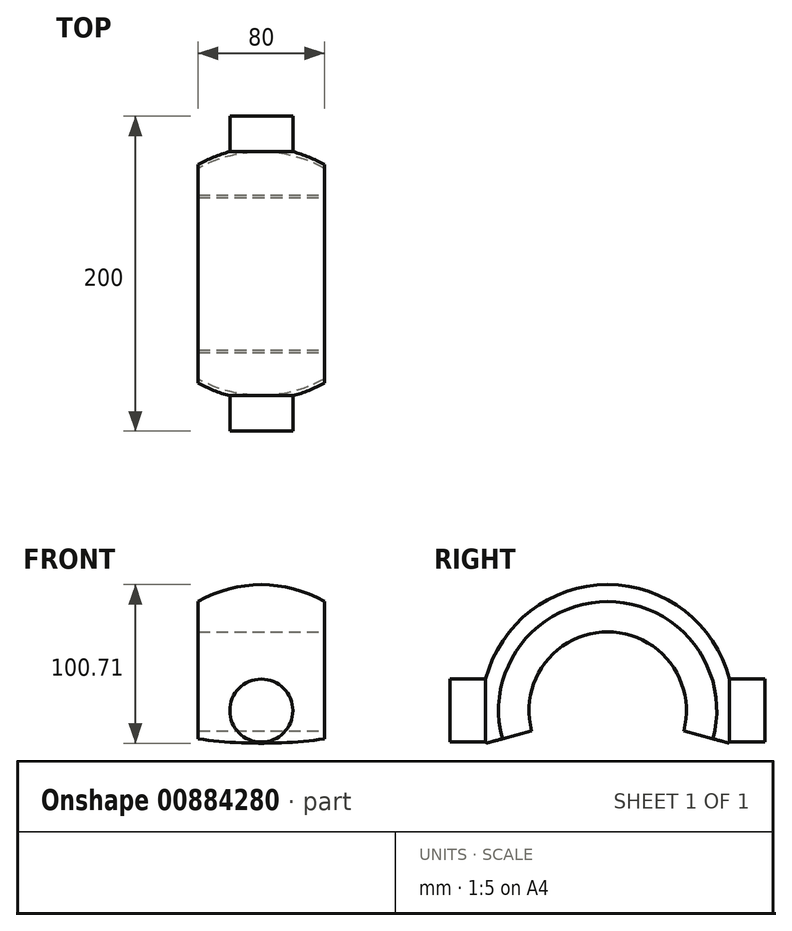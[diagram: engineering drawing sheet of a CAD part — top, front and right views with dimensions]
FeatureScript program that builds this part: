
annotation { "Feature Type Name" : "Feature", "Feature Type Description" : "" }
export const myFeature = defineFeature(function(context is Context, id is Id, definition is map)
    precondition{}
    {
        {
            var Q0;
            Q0=qCreatedBy(makeId("Front.planeOp"),FACE);
            var sketch = newSketch(context, id + "F0", { "sketchPlane" : qUnion([Q0])});
            skLineSegment(sketch, "E0", {"start": v(0, 0) * mm, "end": v(-380.18, 0) * mm, "construction": true});
            skLineSegment(sketch, "E1", {"start": v(-40, 69.28) * mm, "end": v(-40, 50) * mm});
            skLineSegment(sketch, "E2", {"start": v(-40, 50) * mm, "end": v(40, 50) * mm});
            skLineSegment(sketch, "E3", {"start": v(40, 50) * mm, "end": v(40, 69.28) * mm});
            skLineSegment(sketch, "E4", {"start": v(0, 0) * mm, "end": v(0, 237.2) * mm, "construction": true});
            skArc(sketch, "E5", {"start": v(40, 69.28) * mm, "mid": v(0, 80) * mm, "end": v(-40, 69.28) * mm});
            skSolve(sketch);
        }
        {
            var Q0;
            Q0=makeQuery(id+"F0.imprint","IMPRINT",FACE,{"disambiguationData":[TD([[makeQuery(id+"F0.imprint","IMPRINT",EDGE,{"derivedFrom":sQuery(id+"F0.wireOp",EDGE,"E1")}),1.0]])]});
            var Q1;
            Q1=sQuery(id+"F0.wireOp",EDGE,"E0");
            revolve(context, id + "F1", {"surfaceOperationType" : NewSurfaceOperationType.NEW, "entities" : qUnion([Q0]), "axis" : qUnion([Q1]), "revolveType" : RevolveType.SYMMETRIC, "angle" : 210 * degree});
        }
        {
            var Q0;
            Q0=qCreatedBy(makeId("Front.planeOp"),FACE);
            cPlane(context, id + "F2", {"entities" : qUnion([Q0]), "cplaneType" : CPlaneType.OFFSET, "offset" : 100 * mm, "oppositeDirection" : true, "width" : 150 * mm, "height" : 150 * mm});
        }
        {
            var Q0;
            Q0=qCreatedBy(id+"F2.planeOp",FACE);
            var sketch = newSketch(context, id + "F3", { "sketchPlane" : qUnion([Q0])});
            skCircle(sketch, "E6", {"center": v(0, 0) * mm, "radius": 20 * mm});
            skSolve(sketch);
        }
        {
            var Q0;
            Q0=makeQuery(id+"F3.imprint","IMPRINT",FACE,{"disambiguationData":[TD([[makeQuery(id+"F3.imprint","IMPRINT",EDGE,{"derivedFrom":sQuery(id+"F3.wireOp",EDGE,"E6")}),1.0]])]});
            extrude(context, id + "F4", {"entities" : qUnion([Q0]), "operationType" : NewBodyOperationType.ADD, "endBound" : BoundingType.UP_TO_NEXT, "depth" : 25 * mm, "offsetDistance" : 25 * mm});
        }
        {
            var Q0;
            Q0=makeQuery(id+"F1.opRevolve","SWEPT_BODY",BODY,{"disambiguationData":[OSD([sQuery(id+"F0.wireOp",EDGE,"E1"),sQuery(id+"F0.wireOp",EDGE,"E2"),sQuery(id+"F0.wireOp",EDGE,"E3"),sQuery(id+"F0.wireOp",EDGE,"E5")])]});
            var Q1;
            Q1=qCreatedBy(makeId("Front.planeOp"),FACE);
            mirror(context, id + "F5", {"operationType" : NewBodyOperationType.ADD, "entities" : qUnion([Q0]), "mirrorPlane" : qUnion([Q1])});
        }
    });
